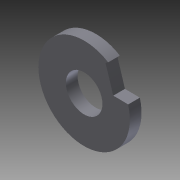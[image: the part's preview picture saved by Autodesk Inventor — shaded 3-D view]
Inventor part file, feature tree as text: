
AUTODESK INVENTOR PART (.ipt)
format: ipt  version: 2014 SP1 (Build 180222100, 222)  size: 89,600 bytes
history: native  units: in
note: dims shown in document units (in); Inventor stores cm internally (conversion verified against a paired STEP export)
features: reference x3, extrude x2, sketch x2
ambient origin geometry x8: Origin, YZ Plane, XZ Plane, XY Plane, X Axis, Y Axis, Z Axis, Center Point
bodies: Solid1 (feature_tree)
feature tree (7):
  extrude  "Extrusion1"  Depth=0.25in
  extrude  "Extrusion2"  Depth=0.08in TaperAngle=0.0deg
  sketch  "Sketch1"  dims[d0=0.625in d1=0.25in]
  sketch  "Sketch2"  dims[d2=0.08in d3=0.0in d4=1.0in d5=0.0in]
  reference  "Reference1"
  reference  "Reference2"
  reference  "Reference3"
